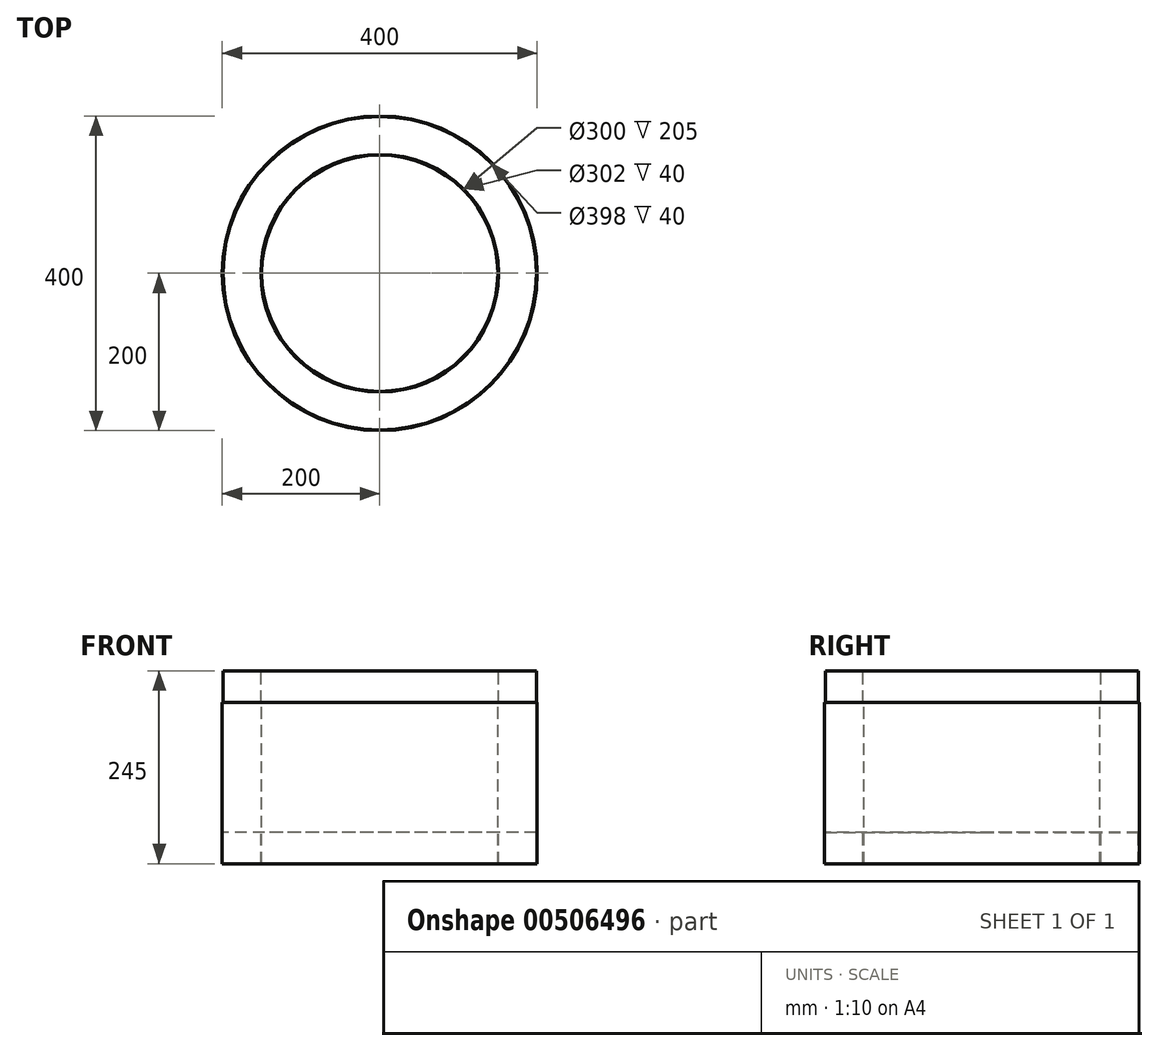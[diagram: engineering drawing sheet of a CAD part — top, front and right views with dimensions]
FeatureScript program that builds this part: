
annotation { "Feature Type Name" : "Feature", "Feature Type Description" : "" }
export const myFeature = defineFeature(function(context is Context, id is Id, definition is map)
    precondition{}
    {
        {
            var Q0;
            Q0=qCreatedBy(makeId("Front.planeOp"),FACE);
            var sketch = newSketch(context, id + "F0", { "sketchPlane" : qUnion([Q0])});
            skLineSegment(sketch, "E0", {"start": v(0, 74.87) * mm, "end": v(0, -73.71) * mm, "construction": true});
            skLineSegment(sketch, "E1", {"start": v(0, 374.84) * mm, "end": v(0, -528.94) * mm, "construction": true});
            skLineSegment(sketch, "E2", {"start": v(-150, -489.75) * mm, "end": v(-150, -284.75) * mm});
            skLineSegment(sketch, "E3", {"start": v(-150, -284.75) * mm, "end": v(-151, -284.75) * mm});
            skLineSegment(sketch, "E4", {"start": v(-151, -284.75) * mm, "end": v(-151, -244.75) * mm});
            skLineSegment(sketch, "E5", {"start": v(-151, -244.75) * mm, "end": v(-199, -244.75) * mm});
            skLineSegment(sketch, "E6", {"start": v(-199, -244.75) * mm, "end": v(-199, -284.75) * mm});
            skLineSegment(sketch, "E7", {"start": v(-199, -284.75) * mm, "end": v(-200, -284.75) * mm});
            skLineSegment(sketch, "E8", {"start": v(-200, -284.75) * mm, "end": v(-200, -489.75) * mm});
            skLineSegment(sketch, "E9", {"start": v(-200, -489.75) * mm, "end": v(-199, -489.75) * mm});
            skLineSegment(sketch, "E10", {"start": v(-199, -489.75) * mm, "end": v(-199, -449.75) * mm});
            skLineSegment(sketch, "E11", {"start": v(-199, -449.75) * mm, "end": v(-151, -449.75) * mm});
            skLineSegment(sketch, "E12", {"start": v(-151, -449.75) * mm, "end": v(-151, -489.75) * mm});
            skLineSegment(sketch, "E13", {"start": v(-151, -489.75) * mm, "end": v(-150, -489.75) * mm});
            skSolve(sketch);
        }
        {
            var Q0;
            Q0=qSketchRegion(id+"F0",true);
            var Q1;
            Q1=sQuery(id+"F0.wireOp",EDGE,"E1");
            revolve(context, id + "F1", {"entities" : qUnion([Q0]), "axis" : qUnion([Q1]), "revolveType" : RevolveType.FULL});
        }
    });
